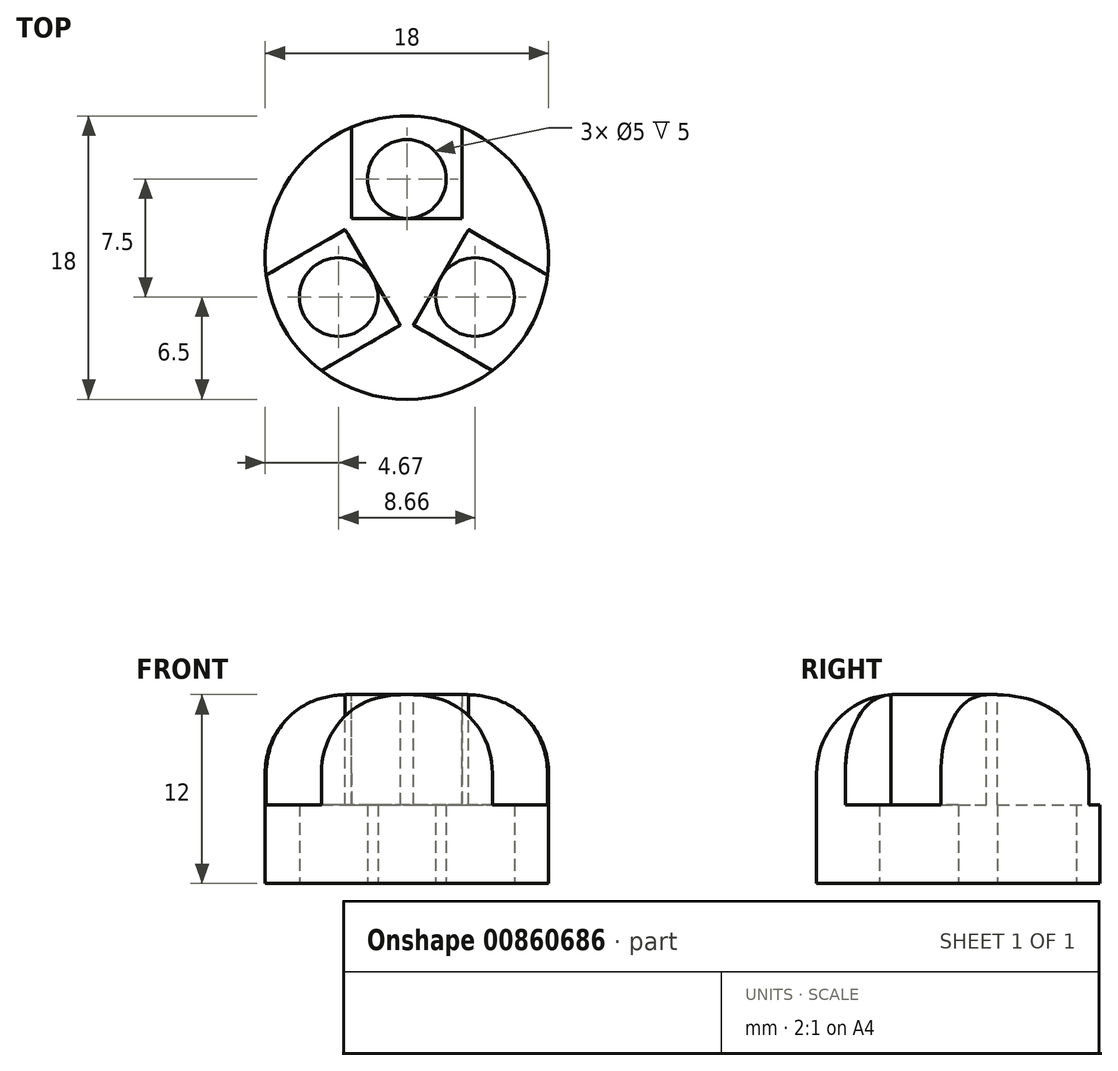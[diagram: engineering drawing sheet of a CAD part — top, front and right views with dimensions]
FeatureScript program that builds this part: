
annotation { "Feature Type Name" : "Feature", "Feature Type Description" : "" }
export const myFeature = defineFeature(function(context is Context, id is Id, definition is map)
    precondition{}
    {
        {
            var Q0;
            Q0=qCreatedBy(makeId("Top.planeOp"),FACE);
            var sketch = newSketch(context, id + "F0", { "sketchPlane" : qUnion([Q0])});
            skCircle(sketch, "E0", {"center": v(0, 0) * mm, "radius": 9 * mm});
            skSolve(sketch);
        }
        {
            var Q0;
            Q0=makeQuery(id+"F0.imprint","IMPRINT",FACE,{"disambiguationData":[TD([[makeQuery(id+"F0.imprint","IMPRINT",EDGE,{"derivedFrom":sQuery(id+"F0.wireOp",EDGE,"E0")}),1.0]])]});
            var sketch = newSketch(context, id + "F1", { "sketchPlane" : qUnion([Q0])});
            skCircle(sketch, "E1", {"center": v(0, 0) * mm, "radius": 5 * mm, "construction": true});
            skCircle(sketch, "E2", {"center": v(0, 5) * mm, "radius": 2.5 * mm});
            skCircle(sketch, "E3.1.0", {"center": v(-4.33, -2.5) * mm, "radius": 2.5 * mm});
            skCircle(sketch, "E3.2.0", {"center": v(4.33, -2.5) * mm, "radius": 2.5 * mm});
            skSolve(sketch);
        }
        {
            var Q0;
            Q0=makeQuery(id+"F0.imprint","IMPRINT",FACE,{"disambiguationData":[TD([[makeQuery(id+"F0.imprint","IMPRINT",EDGE,{"derivedFrom":sQuery(id+"F0.wireOp",EDGE,"E0")}),1.0]])]});
            extrude(context, id + "F2", {"entities" : qUnion([Q0]), "depth" : 12 * mm, "offsetDistance" : 25 * mm});
        }
        {
            var Q0;
            Q0=makeQuery(id+"F1.imprint","IMPRINT",FACE,{"disambiguationData":[TD([[makeQuery(id+"F1.imprint","IMPRINT",EDGE,{"derivedFrom":sQuery(id+"F1.wireOp",EDGE,"E3.1.0")}),1.0]])]});
            var Q1;
            Q1=makeQuery(id+"F1.imprint","IMPRINT",FACE,{"disambiguationData":[TD([[makeQuery(id+"F1.imprint","IMPRINT",EDGE,{"derivedFrom":sQuery(id+"F1.wireOp",EDGE,"E3.2.0")}),1.0]])]});
            var Q2;
            Q2=makeQuery(id+"F1.imprint","IMPRINT",FACE,{"disambiguationData":[TD([[makeQuery(id+"F1.imprint","IMPRINT",EDGE,{"derivedFrom":sQuery(id+"F1.wireOp",EDGE,"E2")}),1.0]])]});
            extrude(context, id + "F3", {"entities" : qUnion([Q0, Q1, Q2]), "operationType" : NewBodyOperationType.REMOVE, "endBound" : BoundingType.THROUGH_ALL, "depth" : 25 * mm, "offsetDistance" : 25 * mm});
        }
        {
            var Q0;
            Q0=makeQuery(id+"F2.opExtrude","CAP_FACE",FACE,{"disambiguationData":[OSD([sQuery(id+"F0.wireOp",EDGE,"E0")])],"isStart":false});
            var sketch = newSketch(context, id + "F4", { "sketchPlane" : qUnion([Q0])});
            skLineSegment(sketch, "E4.bottom", {"start": v(3.5, 2.5) * mm, "end": v(-3.5, 2.5) * mm});
            skLineSegment(sketch, "E4.right", {"start": v(-3.5, 2.5) * mm, "end": v(-3.5, 7.5) * mm});
            skPoint(sketch, "E4.middle", {"position": v(0, 5) * mm});
            skLineSegment(sketch, "E5", {"start": v(3.5, 2.5) * mm, "end": v(3.5, 9.64) * mm});
            skLineSegment(sketch, "E6", {"start": v(3.5, 9.64) * mm, "end": v(-3.5, 9.64) * mm});
            skLineSegment(sketch, "E7", {"start": v(-3.5, 9.64) * mm, "end": v(-3.5, 7.5) * mm});
            skLineSegment(sketch, "E8.1.0", {"start": v(-10.1, -1.8) * mm, "end": v(-6.6, -7.85) * mm});
            skLineSegment(sketch, "E8.1.1", {"start": v(-3.92, 1.78) * mm, "end": v(-10.1, -1.8) * mm});
            skLineSegment(sketch, "E8.1.2", {"start": v(-3.92, 1.78) * mm, "end": v(-0.42, -4.28) * mm});
            skLineSegment(sketch, "E8.1.3", {"start": v(-0.42, -4.28) * mm, "end": v(-4.75, -6.78) * mm});
            skLineSegment(sketch, "E8.1.4", {"start": v(-6.6, -7.85) * mm, "end": v(-4.75, -6.78) * mm});
            skLineSegment(sketch, "E8.2.0", {"start": v(6.6, -7.85) * mm, "end": v(10.1, -1.8) * mm});
            skLineSegment(sketch, "E8.2.1", {"start": v(0.42, -4.28) * mm, "end": v(6.6, -7.85) * mm});
            skLineSegment(sketch, "E8.2.2", {"start": v(0.42, -4.28) * mm, "end": v(3.92, 1.78) * mm});
            skLineSegment(sketch, "E8.2.3", {"start": v(3.92, 1.78) * mm, "end": v(8.25, -0.72) * mm});
            skLineSegment(sketch, "E8.2.4", {"start": v(10.1, -1.8) * mm, "end": v(8.25, -0.72) * mm});
            skPoint(sketch, "E8.center", {"position": v(0, 0) * mm});
            skSolve(sketch);
        }
        {
            var Q0;
            Q0 = qSketchRegion(id + "F4", true);
            extrude(context, id + "F5", {"entities" : qUnion([Q0]), "operationType" : NewBodyOperationType.REMOVE, "oppositeDirection" : true, "depth" : 7 * mm, "offsetDistance" : 25 * mm});
        }
        {
            var Q0;
            {var subQ0=sQuery(id+"F0.wireOp",EDGE,"E0");Q0=makeQuery(id+"F5.boolean.opBoolean","SPLIT",EDGE,{"disambiguationData":[TD([makeQuery(id+"F5.opExtrude","SWEPT_FACE",FACE,{"disambiguationData":[OSD([sQuery(id+"F4.wireOp",EDGE,"E8.1.1")])]})])],"derivedFrom":makeQuery(id+"F2.opExtrude","CAP_EDGE",EDGE,{"disambiguationData":[OSD([subQ0])],"isStart":false})});}
            var Q1;
            {var subQ0=sQuery(id+"F0.wireOp",EDGE,"E0");Q1=makeQuery(id+"F5.boolean.opBoolean","SPLIT",EDGE,{"disambiguationData":[TD([makeQuery(id+"F5.opExtrude","SWEPT_FACE",FACE,{"disambiguationData":[OSD([sQuery(id+"F4.wireOp",EDGE,"E5")])]})])],"derivedFrom":makeQuery(id+"F2.opExtrude","CAP_EDGE",EDGE,{"disambiguationData":[OSD([subQ0])],"isStart":false})});}
            var Q2;
            {var subQ0=sQuery(id+"F0.wireOp",EDGE,"E0");Q2=makeQuery(id+"F5.boolean.opBoolean","SPLIT",EDGE,{"disambiguationData":[TD([makeQuery(id+"F5.opExtrude","SWEPT_FACE",FACE,{"disambiguationData":[OSD([sQuery(id+"F4.wireOp",EDGE,"E8.2.1")])]})])],"derivedFrom":makeQuery(id+"F2.opExtrude","CAP_EDGE",EDGE,{"disambiguationData":[OSD([subQ0])],"isStart":false})});}
            fillet(context, id + "F6", {"entities" : qUnion([Q0, Q1, Q2]), "radius" : 5 * mm, "tangentPropagation" : true, "allowEdgeOverflow" : false});
        }
    });
